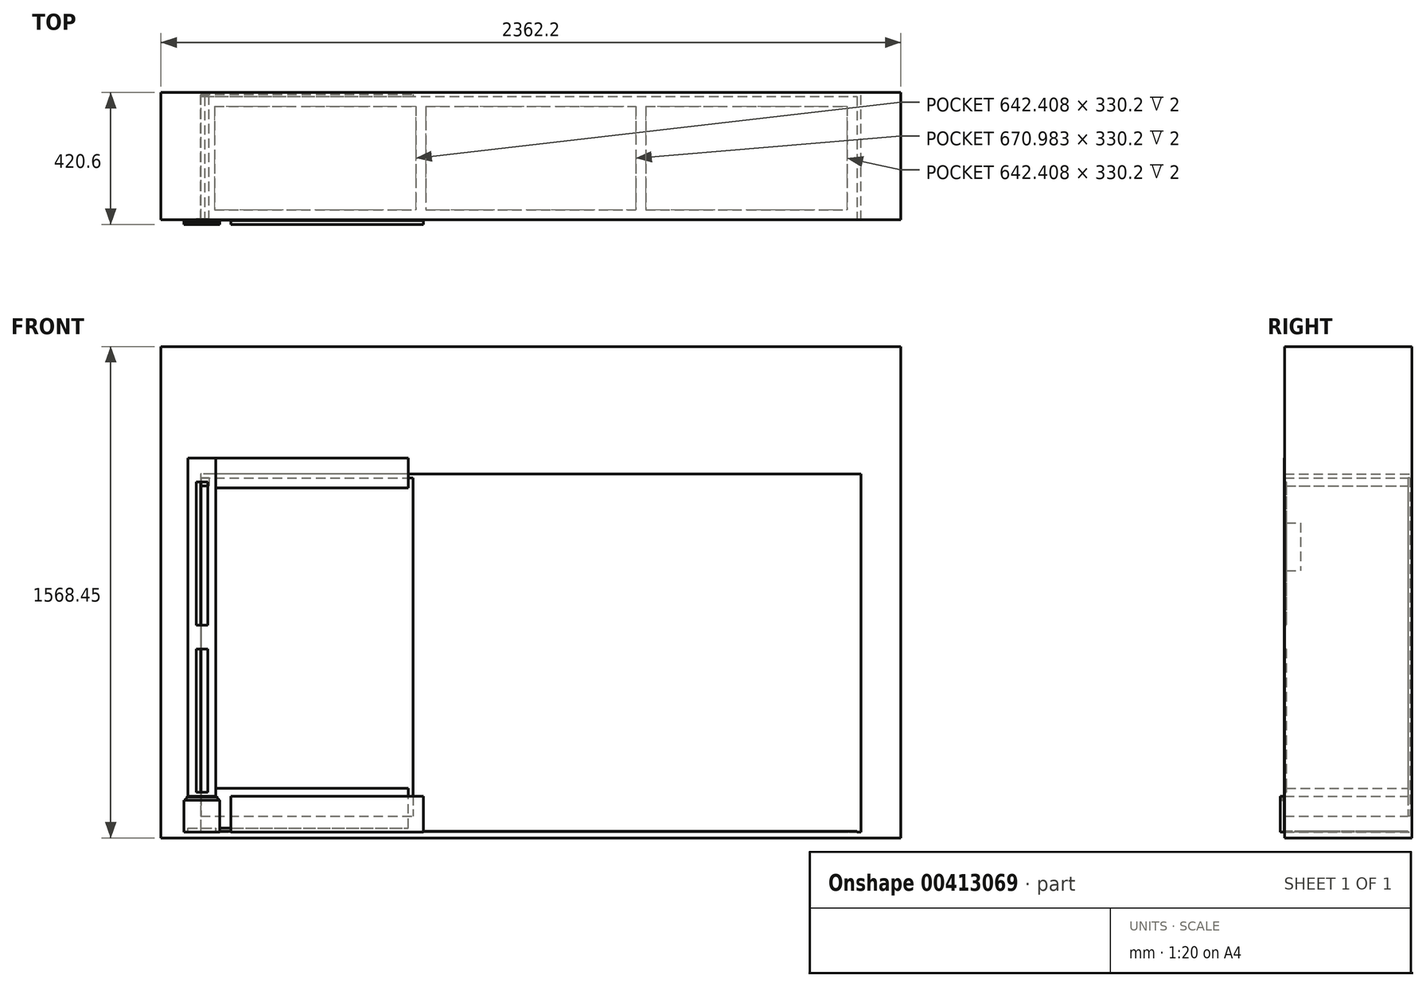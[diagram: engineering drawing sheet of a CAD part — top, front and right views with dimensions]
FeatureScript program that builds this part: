
annotation { "Feature Type Name" : "Feature", "Feature Type Description" : "" }
export const myFeature = defineFeature(function(context is Context, id is Id, definition is map)
    precondition{}
    {
        {
            assignVariable(context, id + "F0", {"name" : "HoleWidth", "anyValue" : 83});
        }
        {
            var Q0;
            Q0=qCreatedBy(makeId("Front.planeOp"),FACE);
            var sketch = newSketch(context, id + "F1", { "sketchPlane" : qUnion([Q0])});
            skLineSegment(sketch, "E0", {"start": v(-1054.1, 0) * mm, "end": v(1054.1, 0) * mm});
            skLineSegment(sketch, "E1", {"start": v(1054.1, 0) * mm, "end": v(1054.1, 1143) * mm});
            skLineSegment(sketch, "E2", {"start": v(1054.1, 1143) * mm, "end": v(-1054.1, 1143) * mm});
            skLineSegment(sketch, "E3", {"start": v(-1054.1, 1143) * mm, "end": v(-1054.1, 0) * mm});
            skLineSegment(sketch, "E4.0", {"start": v(-1181.1, 1549.4) * mm, "end": v(-1181.1, -19.05) * mm});
            skLineSegment(sketch, "E4.1", {"start": v(1181.1, 1549.4) * mm, "end": v(-1181.1, 1549.4) * mm});
            skLineSegment(sketch, "E4.2", {"start": v(1181.1, -19.05) * mm, "end": v(1181.1, 1549.4) * mm});
            skLineSegment(sketch, "E4.3", {"start": v(-1181.1, -19.05) * mm, "end": v(1181.1, -19.05) * mm});
            skPoint(sketch, "E5", {"position": v(0, -19.05) * mm});
            skSolve(sketch);
        }
        {
            var Q0;
            Q0=qSketchRegion(id+"F1",true);
            extrude(context, id + "F2", {"entities" : qUnion([Q0]), "depth" : 406.4 * mm});
        }
        {
            assignVariable(context, id + "F3", {"name" : "Clearence", "anyValue" : .5});
        }
        {
            assignVariable(context, id + "F4", {"name" : "NumberBookcases", "anyValue" : 3});
        }
        {
            assignVariable(context, id + "F5", {"name" : "SideThickness", "anyValue" : .5});
        }
        {
            assignVariable(context, id + "F6", {"name" : "ShelfDadoDepth", "anyValue" : getVariable(context, 'SideThickness') / 3});
        }
        {
            assignVariable(context, id + "F7", {"name" : "StileRecess", "anyValue" : .75});
        }
        {
            assignVariable(context, id + "F8", {"name" : "StileWidth", "anyValue" : 3.5});
        }
        {
            assignVariable(context, id + "F9", {"name" : "SpacerWidth", "anyValue" : getVariable(context, 'StileWidth') - 2 * (getVariable(context, 'SideThickness') + getVariable(context, 'StileRecess'))});
        }
        {
            assignVariable(context, id + "F10", {"name" : "ShelfFixedWidth", "anyValue" : (getVariable(context, 'HoleWidth') - 2 * getVariable(context, 'Clearence') - 2 * getVariable(context, 'NumberBookcases') * (getVariable(context, 'SideThickness') - getVariable(context, 'ShelfDadoDepth')) - (getVariable(context, 'NumberBookcases') - 1) * getVariable(context, 'SpacerWidth')) / getVariable(context, 'NumberBookcases')});
        }
        {
            var Q0;
            Q0=makeQuery(id+"F2.opExtrude","SWEPT_FACE",FACE,{"disambiguationData":[OSD([sQuery(id+"F1.wireOp",EDGE,"E0")])]});
            var sketch = newSketch(context, id + "F11", { "sketchPlane" : qUnion([Q0])});
            skLineSegment(sketch, "E6.bottom", {"start": v(-1009.65, -44.45) * mm, "end": v(-367.24, -44.45) * mm});
            skLineSegment(sketch, "E6.top", {"start": v(-1009.65, -374.65) * mm, "end": v(-367.24, -374.65) * mm});
            skLineSegment(sketch, "E6.left", {"start": v(-1009.65, -44.45) * mm, "end": v(-1009.65, -374.65) * mm});
            skLineSegment(sketch, "E6.right", {"start": v(-367.24, -44.45) * mm, "end": v(-367.24, -374.65) * mm});
            skLineSegment(sketch, "E7.bottom", {"start": v(-335.5, -44.45) * mm, "end": v(335.5, -44.45) * mm});
            skLineSegment(sketch, "E7.top", {"start": v(-335.5, -374.65) * mm, "end": v(335.5, -374.65) * mm});
            skLineSegment(sketch, "E7.left", {"start": v(-335.5, -44.45) * mm, "end": v(-335.5, -374.65) * mm});
            skLineSegment(sketch, "E7.right", {"start": v(335.5, -44.45) * mm, "end": v(335.5, -374.65) * mm});
            skLineSegment(sketch, "E8.bottom", {"start": v(367.24, -44.45) * mm, "end": v(1009.65, -44.45) * mm});
            skLineSegment(sketch, "E8.top", {"start": v(367.24, -374.65) * mm, "end": v(1009.65, -374.65) * mm});
            skLineSegment(sketch, "E8.left", {"start": v(367.24, -44.45) * mm, "end": v(367.24, -374.65) * mm});
            skLineSegment(sketch, "E8.right", {"start": v(1009.65, -44.45) * mm, "end": v(1009.65, -374.65) * mm});
            skLineSegment(sketch, "E9.bottom", {"start": v(-1041.4, -12.7) * mm, "end": v(1041.4, -12.7) * mm});
            skLineSegment(sketch, "E9.top", {"start": v(-1041.4, -406.4) * mm, "end": v(1041.4, -406.4) * mm});
            skLineSegment(sketch, "E9.left", {"start": v(-1041.4, -12.7) * mm, "end": v(-1041.4, -406.4) * mm});
            skLineSegment(sketch, "E9.right", {"start": v(1041.4, -12.7) * mm, "end": v(1041.4, -406.4) * mm});
            skLineSegment(sketch, "E10", {"start": v(0, -406.4) * mm, "end": v(0, 0) * mm, "construction": true});
            skLineSegment(sketch, "E11", {"start": v(0, 0) * mm, "end": v(0, -44.45) * mm, "construction": true});
            skLineSegment(sketch, "E12", {"start": v(-1041.4, -209.55) * mm, "end": v(-1009.65, -209.55) * mm, "construction": true});
            skLineSegment(sketch, "E13", {"start": v(-688.45, -44.45) * mm, "end": v(-688.45, -12.7) * mm, "construction": true});
            skLineSegment(sketch, "E14", {"start": v(-367.24, -209.55) * mm, "end": v(-335.5, -209.55) * mm, "construction": true});
            skPoint(sketch, "E15", {"position": v(246.6, -374.65) * mm});
            skSolve(sketch);
        }
        {
            assignVariable(context, id + "F12", {"name" : "BaseHeight", "anyValue" : 2});
        }
        {
            var Q0;
            Q0 = qSketchRegion(id + "F11", true);
            extrude(context, id + "F13", {"entities" : qUnion([Q0]), "depth" : (getVariable(context, 'BaseHeight')) * mm});
        }
        {
            var Q0;
            Q0=makeQuery(id+"F2.opExtrude","SWEPT_FACE",FACE,{"disambiguationData":[OSD([sQuery(id+"F1.wireOp",EDGE,"E3")])]});
            var sketch = newSketch(context, id + "F14", { "sketchPlane" : qUnion([Q0])});
            skLineSegment(sketch, "E16.bottom", {"start": v(-406.4, 1130.3) * mm, "end": v(-12.7, 1130.3) * mm});
            skLineSegment(sketch, "E16.top", {"start": v(-406.4, 50.8) * mm, "end": v(-12.7, 50.8) * mm});
            skLineSegment(sketch, "E16.left", {"start": v(-406.4, 1130.3) * mm, "end": v(-406.4, 50.8) * mm});
            skLineSegment(sketch, "E16.right", {"start": v(-12.7, 1130.3) * mm, "end": v(-12.7, 50.8) * mm});
            skSolve(sketch);
        }
        {
            var Q0;
            Q0 = qSketchRegion(id + "F14", true);
            extrude(context, id + "F15", {"entities" : qUnion([Q0]), "depth" : (getVariable(context, 'SideThickness')) * mm});
        }
        {
            var Q0;
            Q0=makeQuery(id+"F15.opExtrude","CAP_FACE",FACE,{"disambiguationData":[OSD([sQuery(id+"F14.wireOp",EDGE,"E16.bottom"),sQuery(id+"F14.wireOp",EDGE,"E16.top"),sQuery(id+"F14.wireOp",EDGE,"E16.left"),sQuery(id+"F14.wireOp",EDGE,"E16.right")])],"isStart":false});
            var sketch = newSketch(context, id + "F16", { "sketchPlane" : qUnion([Q0])});
            skLineSegment(sketch, "E17.bottom", {"start": v(-406.4, 139.7) * mm, "end": v(-12.7, 139.7) * mm});
            skLineSegment(sketch, "E17.top", {"start": v(-406.4, 114.3) * mm, "end": v(-12.7, 114.3) * mm});
            skLineSegment(sketch, "E17.left", {"start": v(-406.4, 139.7) * mm, "end": v(-406.4, 114.3) * mm});
            skLineSegment(sketch, "E17.right", {"start": v(-12.7, 139.7) * mm, "end": v(-12.7, 114.3) * mm});
            skLineSegment(sketch, "E18.bottom", {"start": v(-406.4, 1130.3) * mm, "end": v(-12.7, 1130.3) * mm});
            skLineSegment(sketch, "E18.top", {"start": v(-406.4, 1104.9) * mm, "end": v(-12.7, 1104.9) * mm});
            skLineSegment(sketch, "E18.left", {"start": v(-406.4, 1130.3) * mm, "end": v(-406.4, 1104.9) * mm});
            skLineSegment(sketch, "E18.right", {"start": v(-12.7, 1130.3) * mm, "end": v(-12.7, 1104.9) * mm});
            skSolve(sketch);
        }
        {
            var Q0;
            Q0 = qSketchRegion(id + "F16", true);
            extrude(context, id + "F17", {"entities" : qUnion([Q0]), "operationType" : NewBodyOperationType.REMOVE, "oppositeDirection" : true, "depth" : (getVariable(context, 'ShelfDadoDepth')) * mm});
        }
        {
            var Q0;
            Q0=makeQuery(id+"F17.boolean.opBoolean","COPY",FACE,{"derivedFrom":makeQuery(id+"F17.opExtrude","CAP_FACE",FACE,{"disambiguationData":[OSD([sQuery(id+"F16.wireOp",EDGE,"E18.bottom"),sQuery(id+"F16.wireOp",EDGE,"E18.top"),sQuery(id+"F16.wireOp",EDGE,"E18.left"),sQuery(id+"F16.wireOp",EDGE,"E18.right")])],"isStart":false})});
            var sketch = newSketch(context, id + "F18", { "sketchPlane" : qUnion([Q0])});
            skLineSegment(sketch, "E19.bottom", {"start": v(-406.4, 1130.3) * mm, "end": v(-12.7, 1130.3) * mm});
            skLineSegment(sketch, "E19.top", {"start": v(-406.4, 1104.9) * mm, "end": v(-12.7, 1104.9) * mm});
            skLineSegment(sketch, "E19.left", {"start": v(-406.4, 1130.3) * mm, "end": v(-406.4, 1104.9) * mm});
            skLineSegment(sketch, "E19.right", {"start": v(-12.7, 1130.3) * mm, "end": v(-12.7, 1104.9) * mm});
            skSolve(sketch);
        }
        {
            var Q0;
            Q0 = qSketchRegion(id + "F18", true);
            extrude(context, id + "F19", {"entities" : qUnion([Q0]), "depth" : (getVariable(context, 'ShelfFixedWidth')) * mm});
        }
        {
            var Q0;
            {var subQ0=sQuery(id+"F14.wireOp",EDGE,"E16.left");var subQ1=sQuery(id+"F14.wireOp",EDGE,"E16.right");Q0=makeQuery(id+"F17.boolean.opBoolean","SPLIT",FACE,{"disambiguationData":[TD([makeQuery(id+"F17.opExtrude","SWEPT_FACE",FACE,{"disambiguationData":[OSD([sQuery(id+"F16.wireOp",EDGE,"E17.bottom")])]})])],"derivedFrom":makeQuery(id+"F15.opExtrude","CAP_FACE",FACE,{"disambiguationData":[OSD([sQuery(id+"F14.wireOp",EDGE,"E16.bottom"),sQuery(id+"F14.wireOp",EDGE,"E16.top"),subQ0,subQ1])],"isStart":false})});}
            var sketch = newSketch(context, id + "F20", { "sketchPlane" : qUnion([Q0])});
            skLineSegment(sketch, "E20.bottom", {"start": v(-406.4, 986.3) * mm, "end": v(-355.6, 986.3) * mm});
            skLineSegment(sketch, "E20.top", {"start": v(-406.4, 833.9) * mm, "end": v(-355.6, 833.9) * mm});
            skLineSegment(sketch, "E20.left", {"start": v(-406.4, 986.3) * mm, "end": v(-406.4, 833.9) * mm});
            skLineSegment(sketch, "E20.right", {"start": v(-355.6, 986.3) * mm, "end": v(-355.6, 833.9) * mm});
            skSolve(sketch);
        }
        {
            var Q0;
            Q0 = qSketchRegion(id + "F20", true);
            extrude(context, id + "F21", {"entities" : qUnion([Q0]), "depth" : (getVariable(context, 'SpacerWidth')) * mm});
        }
        {
            var Q0;
            Q0=makeQuery(id+"F2.opExtrude","CAP_FACE",FACE,{"disambiguationData":[OSD([sQuery(id+"F1.wireOp",EDGE,"E0"),sQuery(id+"F1.wireOp",EDGE,"E1"),sQuery(id+"F1.wireOp",EDGE,"E2"),sQuery(id+"F1.wireOp",EDGE,"E3"),sQuery(id+"F1.wireOp",EDGE,"E4.0"),sQuery(id+"F1.wireOp",EDGE,"E4.1"),sQuery(id+"F1.wireOp",EDGE,"E4.2"),sQuery(id+"F1.wireOp",EDGE,"E4.3")])],"isStart":false});
            var sketch = newSketch(context, id + "F22", { "sketchPlane" : qUnion([Q0])});
            skLineSegment(sketch, "E21.bottom", {"start": v(-1094.47, 1193.8) * mm, "end": v(-1005.57, 1193.8) * mm});
            skLineSegment(sketch, "E21.top", {"start": v(-1094.47, 12.7) * mm, "end": v(-1005.57, 12.7) * mm});
            skLineSegment(sketch, "E21.left", {"start": v(-1094.47, 1193.8) * mm, "end": v(-1094.47, 12.7) * mm});
            skLineSegment(sketch, "E21.right", {"start": v(-1005.57, 1193.8) * mm, "end": v(-1005.57, 12.7) * mm});
            skSolve(sketch);
        }
        {
            assignVariable(context, id + "F23", {"name" : "StileThickness", "anyValue" : 1.5});
        }
        {
            var Q0;
            Q0 = qSketchRegion(id + "F22", true);
            extrude(context, id + "F24", {"entities" : qUnion([Q0]), "depth" : (getVariable(context, 'StileThickness')) * mm});
        }
        {
            var Q0;
            Q0=makeQuery(id+"F24.opExtrude","CAP_FACE",FACE,{"disambiguationData":[OSD([sQuery(id+"F22.wireOp",EDGE,"E21.bottom"),sQuery(id+"F22.wireOp",EDGE,"E21.top"),sQuery(id+"F22.wireOp",EDGE,"E21.left"),sQuery(id+"F22.wireOp",EDGE,"E21.right")])],"isStart":false});
            var sketch = newSketch(context, id + "F25", { "sketchPlane" : qUnion([Q0])});
            skLineSegment(sketch, "E22.bottom", {"start": v(-1067.95, 1117.6) * mm, "end": v(-1032.08, 1117.6) * mm});
            skLineSegment(sketch, "E22.top", {"start": v(-1067.95, 660.4) * mm, "end": v(-1032.08, 660.4) * mm});
            skLineSegment(sketch, "E22.left", {"start": v(-1067.95, 1117.6) * mm, "end": v(-1067.95, 660.4) * mm});
            skLineSegment(sketch, "E22.right", {"start": v(-1032.08, 1117.6) * mm, "end": v(-1032.08, 660.4) * mm});
            skLineSegment(sketch, "E23.bottom", {"start": v(-1067.95, 584.2) * mm, "end": v(-1032.08, 584.2) * mm});
            skLineSegment(sketch, "E23.top", {"start": v(-1067.95, 127) * mm, "end": v(-1032.08, 127) * mm});
            skLineSegment(sketch, "E23.left", {"start": v(-1067.95, 584.2) * mm, "end": v(-1067.95, 127) * mm});
            skLineSegment(sketch, "E23.right", {"start": v(-1032.08, 584.2) * mm, "end": v(-1032.08, 127) * mm});
            skLineSegment(sketch, "E24", {"start": v(-1050.02, 1117.6) * mm, "end": v(-1050.02, 1193.8) * mm, "construction": true});
            skLineSegment(sketch, "E25", {"start": v(-1050.02, 127) * mm, "end": v(-1050.02, 50.8) * mm, "construction": true});
            skLineSegment(sketch, "E26", {"start": v(-1050.02, 660.4) * mm, "end": v(-1050.02, 584.2) * mm, "construction": true});
            skSolve(sketch);
        }
        {
            var Q0;
            Q0 = qSketchRegion(id + "F25", true);
            extrude(context, id + "F26", {"entities" : qUnion([Q0]), "operationType" : NewBodyOperationType.REMOVE, "oppositeDirection" : true, "depth" : 6.35 * mm});
        }
        {
            var Q0;
            Q0=makeQuery(id+"F2.opExtrude","CAP_FACE",FACE,{"disambiguationData":[OSD([sQuery(id+"F1.wireOp",EDGE,"E0"),sQuery(id+"F1.wireOp",EDGE,"E1"),sQuery(id+"F1.wireOp",EDGE,"E2"),sQuery(id+"F1.wireOp",EDGE,"E3"),sQuery(id+"F1.wireOp",EDGE,"E4.0"),sQuery(id+"F1.wireOp",EDGE,"E4.1"),sQuery(id+"F1.wireOp",EDGE,"E4.2"),sQuery(id+"F1.wireOp",EDGE,"E4.3")])],"isStart":false});
            var sketch = newSketch(context, id + "F27", { "sketchPlane" : qUnion([Q0])});
            skLineSegment(sketch, "E27.bottom", {"start": v(-1005.57, 1193.8) * mm, "end": v(-391.73, 1193.8) * mm});
            skLineSegment(sketch, "E27.top", {"start": v(-1005.57, 1098.55) * mm, "end": v(-391.73, 1098.55) * mm});
            skLineSegment(sketch, "E27.left", {"start": v(-1005.57, 1193.8) * mm, "end": v(-1005.57, 1098.55) * mm});
            skLineSegment(sketch, "E27.right", {"start": v(-391.73, 1193.8) * mm, "end": v(-391.73, 1098.55) * mm});
            skSolve(sketch);
        }
        {
            assignVariable(context, id + "F28", {"name" : "TopRailThickness", "anyValue" : .75});
        }
        {
            var Q0;
            Q0 = qSketchRegion(id + "F27", true);
            var Q1;
            Q1=makeQuery(id+"F24.opExtrude","CAP_FACE",FACE,{"disambiguationData":[OSD([sQuery(id+"F22.wireOp",EDGE,"E21.bottom"),sQuery(id+"F22.wireOp",EDGE,"E21.top"),sQuery(id+"F22.wireOp",EDGE,"E21.left"),sQuery(id+"F22.wireOp",EDGE,"E21.right")])],"isStart":false});
            extrude(context, id + "F29", {"entities" : qUnion([Q0]), "endBoundEntityFace" : qUnion([Q1]), "depth" : (getVariable(context, 'TopRailThickness')) * mm});
        }
        {
            var Q0;
            Q0=makeQuery(id+"F15.opExtrude","SWEPT_FACE",FACE,{"disambiguationData":[OSD([sQuery(id+"F14.wireOp",EDGE,"E16.right")])]});
            var sketch = newSketch(context, id + "F30", { "sketchPlane" : qUnion([Q0])});
            skLineSegment(sketch, "E28.bottom", {"start": v(1054.1, 1130.3) * mm, "end": v(376.77, 1130.3) * mm});
            skLineSegment(sketch, "E28.top", {"start": v(1054.1, 50.8) * mm, "end": v(376.77, 50.8) * mm});
            skLineSegment(sketch, "E28.left", {"start": v(1054.1, 1130.3) * mm, "end": v(1054.1, 50.8) * mm});
            skLineSegment(sketch, "E28.right", {"start": v(376.77, 1130.3) * mm, "end": v(376.77, 50.8) * mm});
            skLineSegment(sketch, "E29", {"start": v(715.43, 1130.3) * mm, "end": v(715.43, 1130.3) * mm});
            skPoint(sketch, "E29.endSnap0", {"position": v(715.43, 1130.3) * mm});
            skSolve(sketch);
        }
        {
            var Q0;
            Q0 = qSketchRegion(id + "F30", true);
            extrude(context, id + "F31", {"entities" : qUnion([Q0]), "depth" : 6.35 * mm});
        }
        {
            var Q0;
            Q0=makeQuery(id+"F29.opExtrude","CAP_FACE",FACE,{"disambiguationData":[OSD([sQuery(id+"F27.wireOp",EDGE,"E27.bottom"),sQuery(id+"F27.wireOp",EDGE,"E27.top"),sQuery(id+"F27.wireOp",EDGE,"E27.left"),sQuery(id+"F27.wireOp",EDGE,"E27.right")])],"isStart":true});
            var sketch = newSketch(context, id + "F32", { "sketchPlane" : qUnion([Q0])});
            skLineSegment(sketch, "E30.bottom", {"start": v(1005.57, 139.7) * mm, "end": v(391.73, 139.7) * mm});
            skLineSegment(sketch, "E30.top", {"start": v(1005.57, 12.7) * mm, "end": v(391.73, 12.7) * mm});
            skLineSegment(sketch, "E30.left", {"start": v(1005.57, 12.7) * mm, "end": v(1005.57, 139.7) * mm});
            skLineSegment(sketch, "E30.right", {"start": v(391.73, 12.7) * mm, "end": v(391.73, 139.7) * mm});
            skSolve(sketch);
        }
        {
            var Q0;
            Q0 = qSketchRegion(id + "F32", true);
            var Q1;
            Q1=makeQuery(id+"F29.opExtrude","CAP_FACE",FACE,{"disambiguationData":[OSD([sQuery(id+"F27.wireOp",EDGE,"E27.bottom"),sQuery(id+"F27.wireOp",EDGE,"E27.top"),sQuery(id+"F27.wireOp",EDGE,"E27.left"),sQuery(id+"F27.wireOp",EDGE,"E27.right")])],"isStart":false});
            extrude(context, id + "F33", {"entities" : qUnion([Q0]), "endBound" : BoundingType.UP_TO_SURFACE, "oppositeDirection" : true, "endBoundEntityFace" : qUnion([Q1]), "depth" : 25.4 * mm});
        }
        {
            var Q0;
            Q0=makeQuery(id+"F24.opExtrude","CAP_FACE",FACE,{"disambiguationData":[OSD([sQuery(id+"F22.wireOp",EDGE,"E21.bottom"),sQuery(id+"F22.wireOp",EDGE,"E21.top"),sQuery(id+"F22.wireOp",EDGE,"E21.left"),sQuery(id+"F22.wireOp",EDGE,"E21.right")])],"isStart":false});
            var sketch = newSketch(context, id + "F34", { "sketchPlane" : qUnion([Q0])});
            skLineSegment(sketch, "E31.bottom", {"start": v(-992.87, 0) * mm, "end": v(-1107.17, 0) * mm});
            skLineSegment(sketch, "E31.top", {"start": v(-992.87, 114.3) * mm, "end": v(-1107.17, 114.3) * mm});
            skLineSegment(sketch, "E31.left", {"start": v(-992.87, 0) * mm, "end": v(-992.87, 114.3) * mm});
            skLineSegment(sketch, "E31.right", {"start": v(-1107.17, 0) * mm, "end": v(-1107.17, 114.3) * mm});
            skLineSegment(sketch, "E32", {"start": v(-1050.02, 12.7) * mm, "end": v(-1050.02, 161.12) * mm, "construction": true});
            skSolve(sketch);
        }
        {
            var Q0;
            Q0 = qSketchRegion(id + "F34", true);
            extrude(context, id + "F35", {"entities" : qUnion([Q0]), "depth" : 12.7 * mm});
        }
        {
            var Q0;
            Q0=makeQuery(id+"F35.opExtrude","CAP_FACE",FACE,{"disambiguationData":[OSD([sQuery(id+"F34.wireOp",EDGE,"E31.bottom"),sQuery(id+"F34.wireOp",EDGE,"E31.top"),sQuery(id+"F34.wireOp",EDGE,"E31.left"),sQuery(id+"F34.wireOp",EDGE,"E31.right")])],"isStart":true});
            var sketch = newSketch(context, id + "F36", { "sketchPlane" : qUnion([Q0])});
            skLineSegment(sketch, "E33.bottom", {"start": v(992.87, 114.3) * mm, "end": v(1005.57, 114.3) * mm});
            skLineSegment(sketch, "E33.top", {"start": v(992.87, 0) * mm, "end": v(1005.57, 0) * mm});
            skLineSegment(sketch, "E33.left", {"start": v(992.87, 114.3) * mm, "end": v(992.87, 0) * mm});
            skLineSegment(sketch, "E33.right", {"start": v(1005.57, 114.3) * mm, "end": v(1005.57, 0) * mm});
            skLineSegment(sketch, "E34.bottom", {"start": v(1107.17, 114.3) * mm, "end": v(1094.47, 114.3) * mm});
            skLineSegment(sketch, "E34.top", {"start": v(1107.17, 0) * mm, "end": v(1094.47, 0) * mm});
            skLineSegment(sketch, "E34.left", {"start": v(1107.17, 114.3) * mm, "end": v(1107.17, 0) * mm});
            skLineSegment(sketch, "E34.right", {"start": v(1094.47, 114.3) * mm, "end": v(1094.47, 0) * mm});
            skSolve(sketch);
        }
        {
            var Q0;
            Q0 = qSketchRegion(id + "F36", true);
            var Q1;
            Q1=makeQuery(id+"F24.opExtrude","CAP_FACE",FACE,{"disambiguationData":[OSD([sQuery(id+"F22.wireOp",EDGE,"E21.bottom"),sQuery(id+"F22.wireOp",EDGE,"E21.top"),sQuery(id+"F22.wireOp",EDGE,"E21.left"),sQuery(id+"F22.wireOp",EDGE,"E21.right")])],"isStart":true});
            extrude(context, id + "F37", {"entities" : qUnion([Q0]), "operationType" : NewBodyOperationType.ADD, "endBound" : BoundingType.UP_TO_SURFACE, "endBoundEntityFace" : qUnion([Q1]), "depth" : 25.4 * mm});
        }
        {
            var Q0;
            Q0=makeQuery(id+"F37.opExtrude","CAP_FACE",FACE,{"disambiguationData":[OSD([sQuery(id+"F36.wireOp",EDGE,"E34.bottom"),sQuery(id+"F36.wireOp",EDGE,"E34.top"),sQuery(id+"F36.wireOp",EDGE,"E34.left"),sQuery(id+"F36.wireOp",EDGE,"E34.right")])],"isStart":false});
            var sketch = newSketch(context, id + "F38", { "sketchPlane" : qUnion([Q0])});
            skLineSegment(sketch, "E35", {"start": v(1097.64, 114.3) * mm, "end": v(1097.64, 111.66) * mm});
            skLineSegment(sketch, "E36", {"start": v(1097.64, 114.3) * mm, "end": v(1107.17, 114.3) * mm});
            skLineSegment(sketch, "E37", {"start": v(1107.17, 114.3) * mm, "end": v(1107.17, 101.6) * mm});
            skLineSegment(sketch, "E38", {"start": v(1107.17, 101.6) * mm, "end": v(1104, 101.6) * mm});
            skFitSpline(sketch, "E39", {"points": [v(1097.64, 111.66) * mm, v(1104, 101.6) * mm], "startDerivative": vector(1.96, -19.53) * mm, "endDerivative": vector(2.07, -19.03) * mm});
            skSolve(sketch);
        }
        {
            var Q0;
            Q0 = qSketchRegion(id + "F38", true);
            var Q1;
            Q1=makeQuery(id+"F37.boolean.opBoolean","MERGE",EDGE,{"derivedFrom":[makeQuery(id+"F35.opExtrude","SWEPT_EDGE",EDGE,{"disambiguationData":[OSD([sQuery(id+"F34.wireOp",EDGE,"E31.top"),sQuery(id+"F34.wireOp",EDGE,"E31.right")])]}),makeQuery(id+"F37.opExtrude","SWEPT_EDGE",EDGE,{"disambiguationData":[OSD([sQuery(id+"F36.wireOp",EDGE,"E34.bottom"),sQuery(id+"F36.wireOp",EDGE,"E34.left")])]})]});
            var Q2;
            Q2=makeQuery(id+"F35.opExtrude","CAP_EDGE",EDGE,{"disambiguationData":[OSD([sQuery(id+"F34.wireOp",EDGE,"E31.top")])],"isStart":false});
            var Q3;
            Q3=makeQuery(id+"F37.boolean.opBoolean","MERGE",EDGE,{"derivedFrom":[makeQuery(id+"F35.opExtrude","SWEPT_EDGE",EDGE,{"disambiguationData":[OSD([sQuery(id+"F34.wireOp",EDGE,"E31.top"),sQuery(id+"F34.wireOp",EDGE,"E31.left")])]}),makeQuery(id+"F37.opExtrude","SWEPT_EDGE",EDGE,{"disambiguationData":[OSD([sQuery(id+"F36.wireOp",EDGE,"E33.bottom"),sQuery(id+"F36.wireOp",EDGE,"E33.left")])]})]});
            sweep(context, id + "F39", {"operationType" : NewBodyOperationType.REMOVE, "profiles" : qUnion([Q0]), "path" : qUnion([Q1, Q2, Q3])});
        }
        {
            var Q0;
            Q0=makeQuery(id+"F35.opExtrude","CAP_FACE",FACE,{"disambiguationData":[OSD([sQuery(id+"F34.wireOp",EDGE,"E31.bottom"),sQuery(id+"F34.wireOp",EDGE,"E31.top"),sQuery(id+"F34.wireOp",EDGE,"E31.left"),sQuery(id+"F34.wireOp",EDGE,"E31.right")])],"isStart":false});
            var sketch = newSketch(context, id + "F40", { "sketchPlane" : qUnion([Q0])});
            skLineSegment(sketch, "E40.bottom", {"start": v(-957.34, 114.3) * mm, "end": v(-343.5, 114.3) * mm});
            skLineSegment(sketch, "E40.top", {"start": v(-957.34, 0) * mm, "end": v(-343.5, 0) * mm});
            skLineSegment(sketch, "E40.left", {"start": v(-957.34, 114.3) * mm, "end": v(-957.34, 0) * mm});
            skLineSegment(sketch, "E40.right", {"start": v(-343.5, 114.3) * mm, "end": v(-343.5, 0) * mm});
            skSolve(sketch);
        }
        {
            var Q0;
            Q0 = qSketchRegion(id + "F40", true);
            var Q1;
            Q1=makeQuery(id+"F35.opExtrude","CAP_FACE",FACE,{"disambiguationData":[OSD([sQuery(id+"F34.wireOp",EDGE,"E31.bottom"),sQuery(id+"F34.wireOp",EDGE,"E31.top"),sQuery(id+"F34.wireOp",EDGE,"E31.left"),sQuery(id+"F34.wireOp",EDGE,"E31.right")])],"isStart":true});
            extrude(context, id + "F41", {"entities" : qUnion([Q0]), "endBound" : BoundingType.UP_TO_SURFACE, "oppositeDirection" : true, "endBoundEntityFace" : qUnion([Q1]), "depth" : 25.4 * mm});
        }
        {
            var Q0;
            Q0=makeQuery(id+"F41.opExtrude","SWEPT_FACE",FACE,{"disambiguationData":[OSD([sQuery(id+"F40.wireOp",EDGE,"E40.left")])]});
            var sketch = newSketch(context, id + "F42", { "sketchPlane" : qUnion([Q0])});
            skFitSpline(sketch, "E41.0.0", {"points": [v(447.68, 111.66) * mm, v(447.7, 111.37) * mm, v(447.78, 110.8) * mm, v(447.95, 110.1) * mm, v(448.12, 109.57) * mm, v(448.33, 109.05) * mm, v(448.59, 108.59) * mm, v(448.89, 108.17) * mm, v(449.21, 107.8) * mm, v(449.65, 107.39) * mm, v(450.2, 106.98) * mm, v(450.78, 106.6) * mm, v(451.35, 106.24) * mm, v(451.91, 105.85) * mm, v(452.36, 105.46) * mm, v(452.7, 105.1) * mm, v(452.94, 104.8) * mm, v(453.16, 104.47) * mm, v(453.35, 104.12) * mm, v(453.53, 103.74) * mm, v(453.67, 103.34) * mm, v(453.8, 102.92) * mm, v(453.93, 102.34) * mm, v(454, 101.9) * mm, v(454.03, 101.6) * mm]});
            skLineSegment(sketch, "E42.0.0", {"start": v(447.68, 114.3) * mm, "end": v(447.68, 111.66) * mm});
            skLineSegment(sketch, "E43", {"start": v(454.03, 101.6) * mm, "end": v(457.2, 101.6) * mm});
            skLineSegment(sketch, "E44", {"start": v(457.2, 101.6) * mm, "end": v(457.2, 114.3) * mm});
            skLineSegment(sketch, "E45", {"start": v(457.2, 114.3) * mm, "end": v(447.68, 114.3) * mm});
            skSolve(sketch);
        }
        {
            var Q0;
            Q0 = qSketchRegion(id + "F42", true);
            extrude(context, id + "F43", {"entities" : qUnion([Q0]), "operationType" : NewBodyOperationType.REMOVE, "endBound" : BoundingType.THROUGH_ALL, "oppositeDirection" : true, "depth" : 25.4 * mm});
        }
        {
            var Q0;
            Q0=makeQuery(id+"F19.opExtrude","CAP_FACE",FACE,{"disambiguationData":[OSD([sQuery(id+"F18.wireOp",EDGE,"E19.bottom"),sQuery(id+"F18.wireOp",EDGE,"E19.top"),sQuery(id+"F18.wireOp",EDGE,"E19.left"),sQuery(id+"F18.wireOp",EDGE,"E19.right")])],"isStart":false});
            var sketch = newSketch(context, id + "F44", { "sketchPlane" : qUnion([Q0])});
            skLineSegment(sketch, "E46.bottom", {"start": v(-406.4, 1130.3) * mm, "end": v(-12.7, 1130.3) * mm});
            skLineSegment(sketch, "E46.top", {"start": v(-406.4, 1104.9) * mm, "end": v(-12.7, 1104.9) * mm});
            skLineSegment(sketch, "E46.left", {"start": v(-406.4, 1130.3) * mm, "end": v(-406.4, 1104.9) * mm});
            skLineSegment(sketch, "E46.right", {"start": v(-12.7, 1130.3) * mm, "end": v(-12.7, 1104.9) * mm});
            skSolve(sketch);
        }
        {
            var Q0;
            Q0 = qSketchRegion(id + "F44", true);
            extrude(context, id + "F45", {"entities" : qUnion([Q0]), "oppositeDirection" : true, "depth" : (getVariable(context, 'ShelfFixedWidth') - 2 * getVariable(context, 'ShelfDadoDepth')) * mm});
        }
    });
